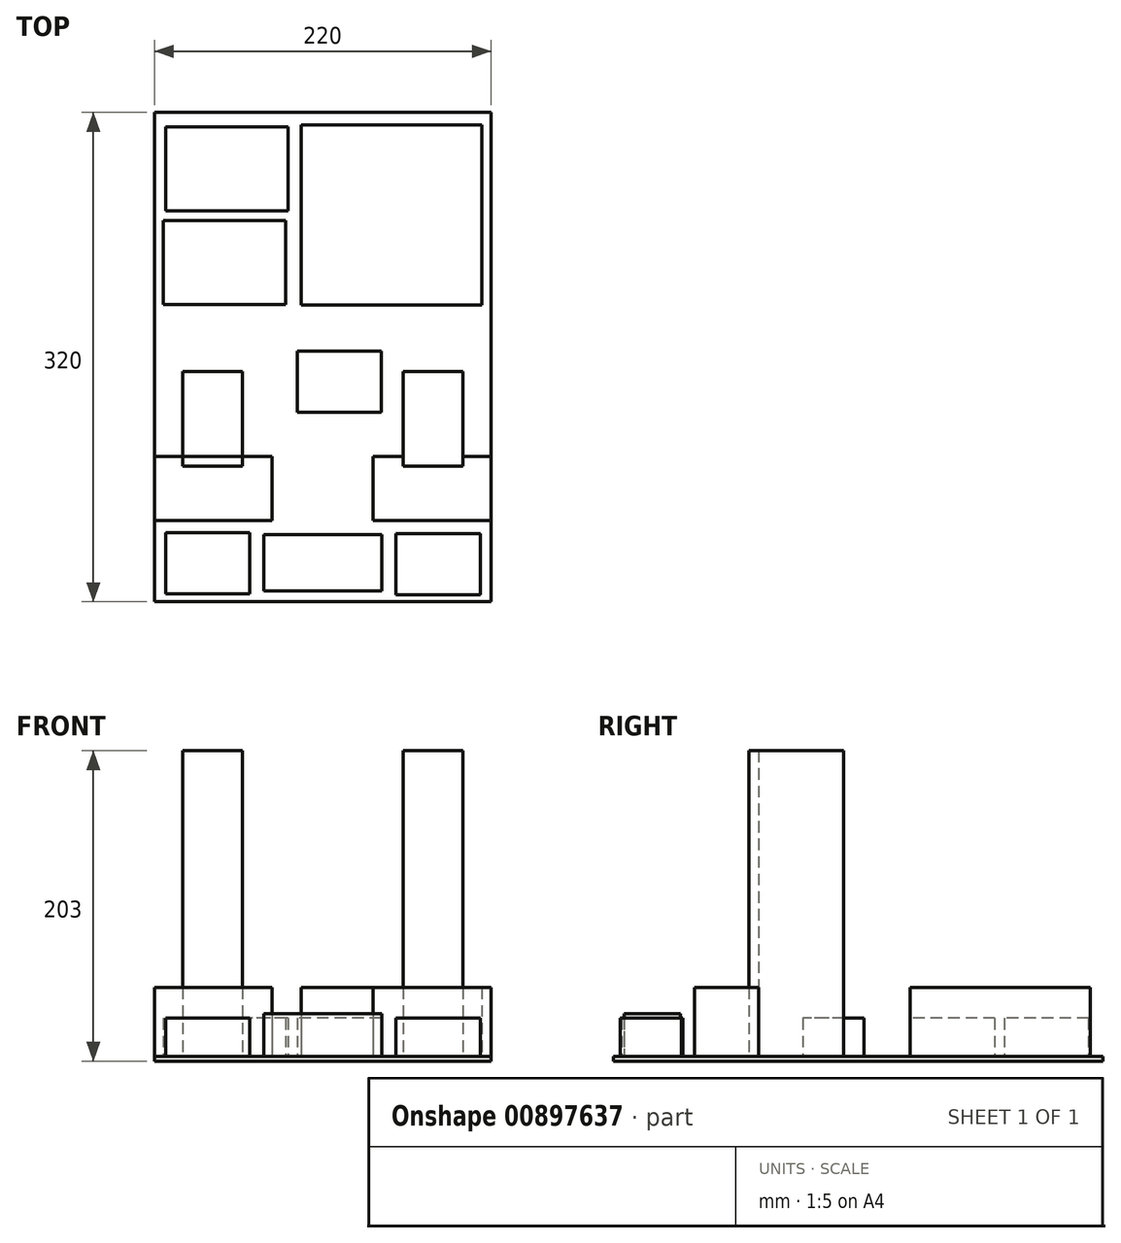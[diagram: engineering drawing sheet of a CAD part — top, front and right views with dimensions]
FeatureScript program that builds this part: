
annotation { "Feature Type Name" : "Feature", "Feature Type Description" : "" }
export const myFeature = defineFeature(function(context is Context, id is Id, definition is map)
    precondition{}
    {
        {
            var Q0;
            Q0=qCreatedBy(makeId("Top.planeOp"),FACE);
            var sketch = newSketch(context, id + "F0", { "sketchPlane" : qUnion([Q0])});
            skLineSegment(sketch, "E0.bottom", {"start": v(0, 0) * mm, "end": v(220, 0) * mm});
            skLineSegment(sketch, "E0.top", {"start": v(0, 320) * mm, "end": v(220, 320) * mm});
            skLineSegment(sketch, "E0.left", {"start": v(0, 0) * mm, "end": v(0, 320) * mm});
            skLineSegment(sketch, "E0.right", {"start": v(220, 0) * mm, "end": v(220, 320) * mm});
            skSolve(sketch);
        }
        {
            var Q0;
            Q0=makeQuery(id+"F0.imprint","IMPRINT",FACE,{"disambiguationData":[TD([[makeQuery(id+"F0.imprint","IMPRINT",EDGE,{"derivedFrom":sQuery(id+"F0.wireOp",EDGE,"E0.bottom")}),1.0]])]});
            extrude(context, id + "F1", {"entities" : qUnion([Q0]), "depth" : 3 * mm, "offsetDistance" : 25 * mm});
        }
        {
            var Q0;
            Q0=makeQuery(id+"F1.opExtrude","CAP_FACE",FACE,{"disambiguationData":[OSD([sQuery(id+"F0.wireOp",EDGE,"E0.bottom"),sQuery(id+"F0.wireOp",EDGE,"E0.top"),sQuery(id+"F0.wireOp",EDGE,"E0.left"),sQuery(id+"F0.wireOp",EDGE,"E0.right")])],"isStart":false});
            var sketch = newSketch(context, id + "F2", { "sketchPlane" : qUnion([Q0])});
            skLineSegment(sketch, "E1.bottom", {"start": v(0, 95) * mm, "end": v(77, 95) * mm});
            skLineSegment(sketch, "E1.top", {"start": v(0, 53) * mm, "end": v(77, 53) * mm});
            skLineSegment(sketch, "E1.left", {"start": v(0, 95) * mm, "end": v(0, 53) * mm});
            skLineSegment(sketch, "E1.right", {"start": v(77, 95) * mm, "end": v(77, 53) * mm});
            skLineSegment(sketch, "E2", {"start": v(110, 320) * mm, "end": v(110, 0) * mm, "construction": true});
            skLineSegment(sketch, "E3.bottom", {"start": v(213.93, 311.97) * mm, "end": v(95.93, 311.97) * mm});
            skLineSegment(sketch, "E3.top", {"start": v(213.93, 193.97) * mm, "end": v(95.93, 193.97) * mm});
            skLineSegment(sketch, "E3.left", {"start": v(213.93, 311.97) * mm, "end": v(213.93, 193.97) * mm});
            skLineSegment(sketch, "E3.right", {"start": v(95.93, 311.97) * mm, "end": v(95.93, 193.97) * mm});
            skPoint(sketch, "E3.middle", {"position": v(154.93, 252.97) * mm});
            skLineSegment(sketch, "E4.bottom", {"start": v(148.5, 43.95) * mm, "end": v(71.5, 43.95) * mm});
            skLineSegment(sketch, "E4.top", {"start": v(148.5, 6.95) * mm, "end": v(71.5, 6.95) * mm});
            skLineSegment(sketch, "E4.left", {"start": v(148.5, 43.95) * mm, "end": v(148.5, 6.95) * mm});
            skLineSegment(sketch, "E4.right", {"start": v(71.5, 43.95) * mm, "end": v(71.5, 6.95) * mm});
            skPoint(sketch, "E4.middle", {"position": v(110, 25.45) * mm});
            skLineSegment(sketch, "E5.bottom", {"start": v(85.8, 249.41) * mm, "end": v(5.8, 249.41) * mm});
            skLineSegment(sketch, "E5.top", {"start": v(85.8, 194.41) * mm, "end": v(5.8, 194.41) * mm});
            skLineSegment(sketch, "E5.left", {"start": v(85.8, 249.41) * mm, "end": v(85.8, 194.41) * mm});
            skLineSegment(sketch, "E5.right", {"start": v(5.8, 249.41) * mm, "end": v(5.8, 194.41) * mm});
            skPoint(sketch, "E5.middle", {"position": v(45.8, 221.91) * mm});
            skLineSegment(sketch, "E6.bottom", {"start": v(87.24, 310.69) * mm, "end": v(7.24, 310.69) * mm});
            skLineSegment(sketch, "E6.top", {"start": v(87.24, 255.69) * mm, "end": v(7.24, 255.69) * mm});
            skLineSegment(sketch, "E6.left", {"start": v(87.24, 310.69) * mm, "end": v(87.24, 255.69) * mm});
            skLineSegment(sketch, "E6.right", {"start": v(7.24, 310.69) * mm, "end": v(7.24, 255.69) * mm});
            skPoint(sketch, "E6.middle", {"position": v(47.24, 283.19) * mm});
            skLineSegment(sketch, "E7.bottom", {"start": v(212.92, 44.61) * mm, "end": v(157.92, 44.61) * mm});
            skLineSegment(sketch, "E7.top", {"start": v(212.92, 4.61) * mm, "end": v(157.92, 4.61) * mm});
            skLineSegment(sketch, "E7.left", {"start": v(212.92, 44.61) * mm, "end": v(212.92, 4.61) * mm});
            skLineSegment(sketch, "E7.right", {"start": v(157.92, 44.61) * mm, "end": v(157.92, 4.61) * mm});
            skPoint(sketch, "E7.middle", {"position": v(185.42, 24.61) * mm});
            skLineSegment(sketch, "E8.bottom", {"start": v(62.26, 45.28) * mm, "end": v(7.26, 45.28) * mm});
            skLineSegment(sketch, "E8.top", {"start": v(62.26, 5.28) * mm, "end": v(7.26, 5.28) * mm});
            skLineSegment(sketch, "E8.left", {"start": v(62.26, 45.28) * mm, "end": v(62.26, 5.28) * mm});
            skLineSegment(sketch, "E8.right", {"start": v(7.26, 45.28) * mm, "end": v(7.26, 5.28) * mm});
            skPoint(sketch, "E8.middle", {"position": v(34.76, 25.28) * mm});
            skLineSegment(sketch, "E9.bottom", {"start": v(57.5, 150.6) * mm, "end": v(18.5, 150.6) * mm});
            skLineSegment(sketch, "E9.top", {"start": v(57.5, 88.6) * mm, "end": v(18.5, 88.6) * mm});
            skLineSegment(sketch, "E9.left", {"start": v(57.5, 150.6) * mm, "end": v(57.5, 88.6) * mm});
            skLineSegment(sketch, "E9.right", {"start": v(18.5, 150.6) * mm, "end": v(18.5, 88.6) * mm});
            skPoint(sketch, "E9.middle", {"position": v(38, 119.6) * mm});
            skLineSegment(sketch, "E10.MirrorCS", {"start": v(220, 95) * mm, "end": v(220, 53) * mm});
            skLineSegment(sketch, "E11.MirrorCS", {"start": v(220, 53) * mm, "end": v(143, 53) * mm});
            skLineSegment(sketch, "E12.MirrorCS", {"start": v(143, 95) * mm, "end": v(143, 53) * mm});
            skLineSegment(sketch, "E13.MirrorCS", {"start": v(220, 95) * mm, "end": v(143, 95) * mm});
            skLineSegment(sketch, "E14.MirrorCS", {"start": v(162.5, 150.6) * mm, "end": v(162.5, 88.6) * mm});
            skLineSegment(sketch, "E15.MirrorCS", {"start": v(201.5, 150.6) * mm, "end": v(201.5, 88.6) * mm});
            skLineSegment(sketch, "E16.MirrorCS", {"start": v(162.5, 150.6) * mm, "end": v(201.5, 150.6) * mm});
            skLineSegment(sketch, "E17.MirrorCS", {"start": v(162.5, 88.6) * mm, "end": v(201.5, 88.6) * mm});
            skPoint(sketch, "E18.MirrorP", {"position": v(182, 119.6) * mm});
            skLineSegment(sketch, "E19.bottom", {"start": v(148.26, 163.93) * mm, "end": v(93.26, 163.93) * mm});
            skLineSegment(sketch, "E19.top", {"start": v(148.26, 123.93) * mm, "end": v(93.26, 123.93) * mm});
            skLineSegment(sketch, "E19.left", {"start": v(148.26, 163.93) * mm, "end": v(148.26, 123.93) * mm});
            skLineSegment(sketch, "E19.right", {"start": v(93.26, 163.93) * mm, "end": v(93.26, 123.93) * mm});
            skPoint(sketch, "E19.middle", {"position": v(120.76, 143.93) * mm});
            skPoint(sketch, "E20", {"position": v(0, 160) * mm});
            skSolve(sketch);
        }
        {
            var Q0;
            Q0=makeQuery(id+"F2.imprint","IMPRINT",FACE,{"disambiguationData":[TD([[makeQuery(id+"F2.imprint","IMPRINT",EDGE,{"derivedFrom":sQuery(id+"F2.wireOp",EDGE,"E3.bottom")}),1.0]])]});
            extrude(context, id + "F3", {"entities" : qUnion([Q0]), "depth" : 45 * mm, "offsetDistance" : 25 * mm});
        }
        {
            var Q0;
            Q0=makeQuery(id+"F2.imprint","IMPRINT",FACE,{"disambiguationData":[TD([[makeQuery(id+"F2.imprint","IMPRINT",EDGE,{"derivedFrom":sQuery(id+"F2.wireOp",EDGE,"E14.MirrorCS")}),1.0]])]});
            var Q1;
            Q1=makeQuery(id+"F2.imprint","IMPRINT",FACE,{"disambiguationData":[TD([[makeQuery(id+"F2.imprint","IMPRINT",EDGE,{"derivedFrom":sQuery(id+"F2.wireOp",EDGE,"E9.bottom")}),1.0]])]});
            extrude(context, id + "F4", {"entities" : qUnion([Q0, Q1]), "depth" : 200 * mm, "offsetDistance" : 25 * mm});
        }
        {
            var Q0;
            Q0=makeQuery(id+"F2.imprint","IMPRINT",FACE,{"disambiguationData":[TD([[makeQuery(id+"F2.imprint","IMPRINT",EDGE,{"derivedFrom":sQuery(id+"F2.wireOp",EDGE,"E19.bottom")}),1.0]])]});
            var Q1;
            Q1=makeQuery(id+"F2.imprint","IMPRINT",FACE,{"disambiguationData":[TD([[makeQuery(id+"F2.imprint","IMPRINT",EDGE,{"derivedFrom":sQuery(id+"F2.wireOp",EDGE,"E8.bottom")}),1.0]])]});
            var Q2;
            Q2=makeQuery(id+"F2.imprint","IMPRINT",FACE,{"disambiguationData":[TD([[makeQuery(id+"F2.imprint","IMPRINT",EDGE,{"derivedFrom":sQuery(id+"F2.wireOp",EDGE,"E7.bottom")}),1.0]])]});
            extrude(context, id + "F5", {"entities" : qUnion([Q0, Q1, Q2]), "depth" : 25 * mm, "offsetDistance" : 25 * mm});
        }
        {
            var Q0;
            Q0=makeQuery(id+"F2.imprint","IMPRINT",FACE,{"disambiguationData":[TD([[makeQuery(id+"F2.imprint","IMPRINT",EDGE,{"derivedFrom":sQuery(id+"F2.wireOp",EDGE,"E6.bottom")}),1.0]])]});
            var Q1;
            Q1=makeQuery(id+"F2.imprint","IMPRINT",FACE,{"disambiguationData":[TD([[makeQuery(id+"F2.imprint","IMPRINT",EDGE,{"derivedFrom":sQuery(id+"F2.wireOp",EDGE,"E5.bottom")}),1.0]])]});
            extrude(context, id + "F6", {"entities" : qUnion([Q0, Q1]), "depth" : 25 * mm, "offsetDistance" : 25 * mm});
        }
        {
            var Q0;
            Q0=makeQuery(id+"F2.imprint","IMPRINT",FACE,{"disambiguationData":[TD([[makeQuery(id+"F2.imprint","IMPRINT",EDGE,{"derivedFrom":sQuery(id+"F2.wireOp",EDGE,"E1.bottom")}),-1.0]])]});
            var Q1;
            Q1=makeQuery(id+"F2.imprint","IMPRINT",FACE,{"disambiguationData":[TD([[makeQuery(id+"F2.imprint","IMPRINT",EDGE,{"derivedFrom":sQuery(id+"F2.wireOp",EDGE,"E10.MirrorCS")}),1.0]])]});
            extrude(context, id + "F7", {"entities" : qUnion([Q0, Q1]), "depth" : 45 * mm, "offsetDistance" : 25 * mm});
        }
        {
            var Q0;
            Q0=makeQuery(id+"F2.imprint","IMPRINT",FACE,{"disambiguationData":[TD([[makeQuery(id+"F2.imprint","IMPRINT",EDGE,{"derivedFrom":sQuery(id+"F2.wireOp",EDGE,"E4.bottom")}),1.0]])]});
            extrude(context, id + "F8", {"entities" : qUnion([Q0]), "depth" : 28 * mm, "offsetDistance" : 25 * mm});
        }
    });
